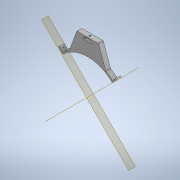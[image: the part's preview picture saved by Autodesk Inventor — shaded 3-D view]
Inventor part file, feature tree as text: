
AUTODESK INVENTOR PART (.ipt)
format: ipt  version: 2021.1 (Build 251245010, 245A)  size: 241,664 bytes
history: native  units: in
note: dims shown in document units (in); Inventor stores cm internally (conversion verified against a paired STEP export)
features: sketch x11, extrude x8, hole x2, plane x2, fillet x2, split x2, pattern_circular x1
ambient origin geometry x8: Origin, YZ Plane, XZ Plane, XY Plane, X Axis, Y Axis, Z Axis, Center Point
bodies: Solid1 (feature_tree)
feature tree (28):
  extrude  "Extrusion1"  Depth=0.75in TaperAngle=0.0deg
  extrude  "Extrusion2"  TaperAngle=0.0deg  [1 undecoded]
  extrude  "Extrusion3"  TaperAngle=45.0deg  [1 undecoded]
  extrude  "Extrusion4"  TaperAngle=45.0deg  [1 undecoded]
  sketch  "Sketch6"  dims[d47=0.25in d48=45.0deg]
  hole  "Hole2"  [1 undecoded]
  plane  "Work Plane1"
  plane  "Work Plane2"
  extrude  "Extrusion7"  Depth=0.25in TaperAngle=360.0deg
  hole  "Hole4"  [1 undecoded]
  pattern_circular  "Circular Pattern1"  Angle=30.0deg  [1 undecoded]
  extrude  "Extrusion8"  TaperAngle=30.0deg  [1 undecoded]
  sketch  "Sketch14"  dims[d65=0.0in d66=0.0in]
  extrude  "Extrusion9"  Depth=0.75in
  extrude  "Extrusion10"  TaperAngle=0.0deg  [1 undecoded]
  fillet  "Fillet1"  Radius=0.125in
  fillet  "Fillet2"  Radius=0.125in
  split  "Split3"
  split  "Split4"
  sketch  "Sketch1"  dims[d3=0.0in d7=0.75in d8=0.0in]
  sketch  "Sketch2"  dims[d9=2.5in d10=0.0in d22=0.0in]
  sketch  "Sketch5"  dims[d31=0.266in d32=0.75in d33=0.507in d34=0.25in d35=0.5635in d36=1.0in d37=0.8108in d45=45.0deg d46=-0.3092in]
  sketch  "Sketch7"  dims[d49=1.0in d50=135.0deg]
  sketch  "Sketch11"  dims[d51=0.75in d52=0.0in]
  sketch  "Sketch12"  dims[d53=0.201in d54=0.75in d55=0.507in d56=0.25in d57=0.5635in d58=1.0in d59=0.8108in d60=1.5748in d61=360.0deg]
  sketch  "Sketch13"  dims[d63=0.35in d64=0.1in]
  sketch  "Sketch15"  dims[d67=0.75in]
  sketch  "Sketch16"  dims[d68=0.0in d69=30.0deg d70=30.0deg d71=0.75in d72=0.0in d73=0.125in d74=0.125in]
note: 8 required parameter values undecoded (feature->parameter linkage not recoverable at this tier; creation-order binding heuristic only, values carry confidence <= 0.55)
